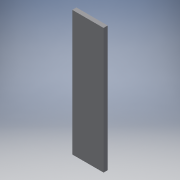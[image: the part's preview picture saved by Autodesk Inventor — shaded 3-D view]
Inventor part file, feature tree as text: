
AUTODESK INVENTOR PART (.ipt)
format: ipt  version: 2018 (Build 220112000, 112)  size: 91,136 bytes
history: native  units: mm
features: other x1, extrude x1, sketch x1
ambient origin geometry x8: Origin, YZ Plane, XZ Plane, XY Plane, X Axis, Y Axis, Z Axis, Center Point
bodies: Body1 (feature_tree)
feature tree (3):
  other  "ソリッド1"
  extrude  "押し出し1"  Depth=30.0mm
  sketch  "スケッチ1"
